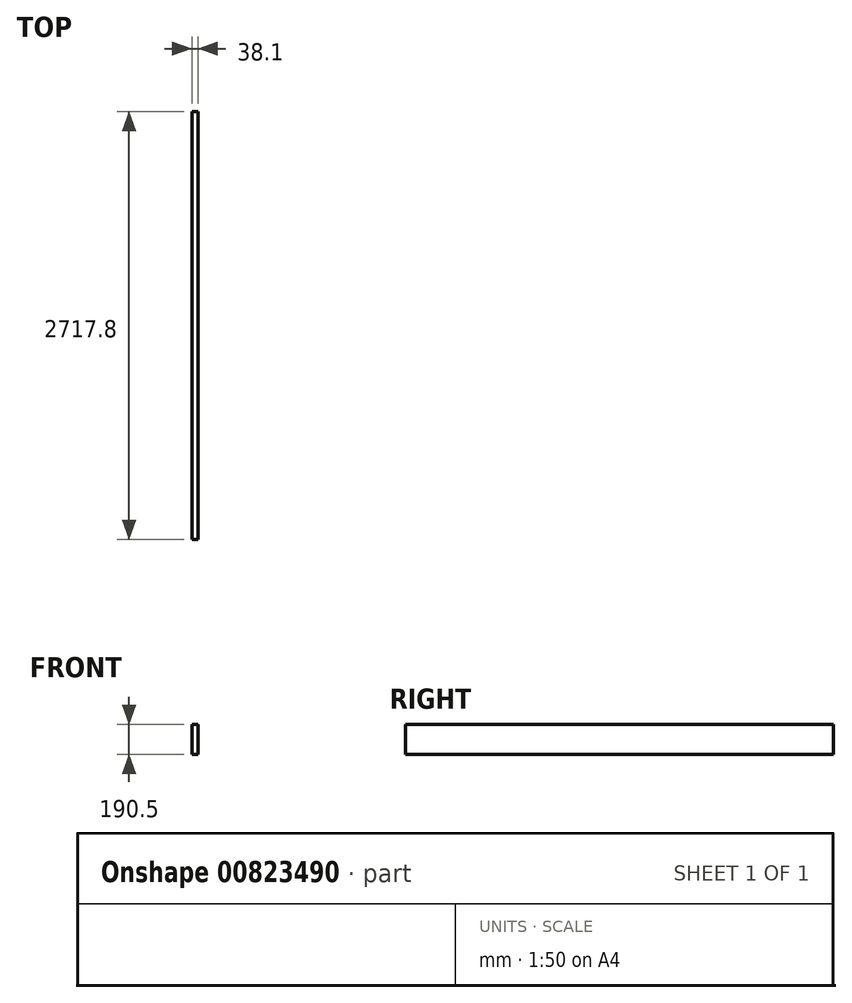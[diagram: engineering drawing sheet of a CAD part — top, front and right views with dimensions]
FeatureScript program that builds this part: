
annotation { "Feature Type Name" : "Feature", "Feature Type Description" : "" }
export const myFeature = defineFeature(function(context is Context, id is Id, definition is map)
    precondition{}
    {
        {
            var Q0;
            Q0=qCreatedBy(makeId("Front.planeOp"),FACE);
            var sketch = newSketch(context, id + "F0", { "sketchPlane" : qUnion([Q0])});
            skLineSegment(sketch, "E0.bottom", {"start": v(0, 0) * mm, "end": v(38.1, 0) * mm});
            skLineSegment(sketch, "E0.top", {"start": v(0, 190.5) * mm, "end": v(38.1, 190.5) * mm});
            skLineSegment(sketch, "E0.left", {"start": v(0, 0) * mm, "end": v(0, 190.5) * mm});
            skLineSegment(sketch, "E0.right", {"start": v(38.1, 0) * mm, "end": v(38.1, 190.5) * mm});
            skSolve(sketch);
        }
        {
            var Q0;
            Q0=qSketchRegion(id+"F0",true);
            extrude(context, id + "F1", {"entities" : qUnion([Q0]), "depth" : 2717.8 * mm, "offsetDistance" : 25.4 * mm});
        }
    });
